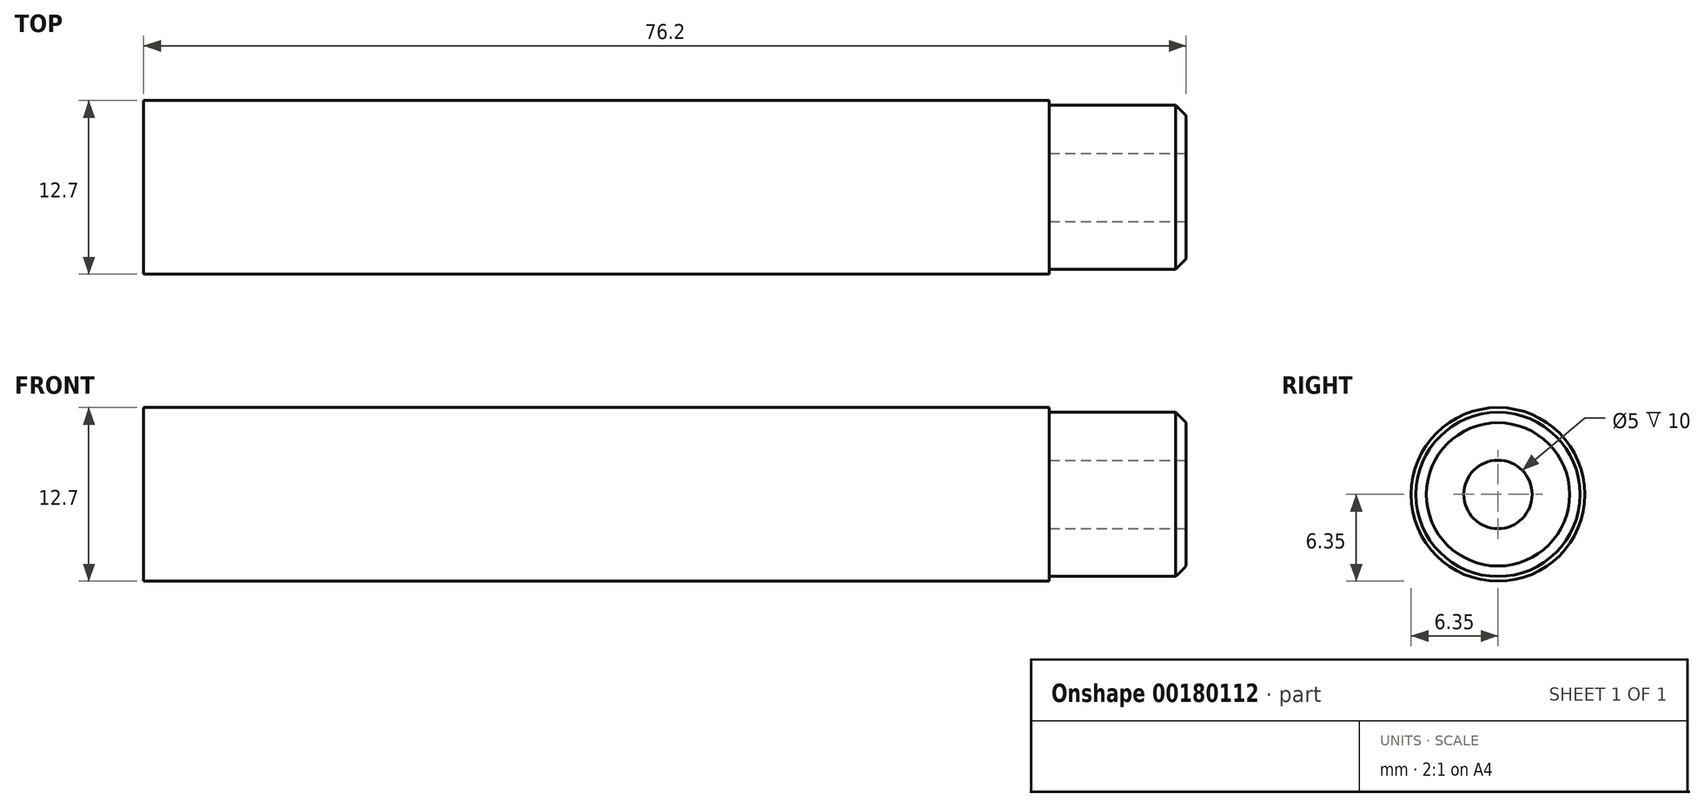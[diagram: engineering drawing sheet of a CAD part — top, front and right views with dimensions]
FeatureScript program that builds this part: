
annotation { "Feature Type Name" : "Feature", "Feature Type Description" : "" }
export const myFeature = defineFeature(function(context is Context, id is Id, definition is map)
    precondition{}
    {
        {
            var Q0;
            Q0=qCreatedBy(makeId("Right.planeOp"),FACE);
            var sketch = newSketch(context, id + "F0", { "sketchPlane" : qUnion([Q0])});
            skCircle(sketch, "E0", {"center": v(0, 0) * mm, "radius": 6 * mm});
            skSolve(sketch);
        }
        {
            var Q0;
            Q0=qSketchRegion(id+"F0",true);
            extrude(context, id + "F1", {"entities" : qUnion([Q0]), "depth" : 76.2 * mm});
        }
        {
            var Q0;
            Q0=makeQuery(id+"F1.opExtrude","CAP_EDGE",EDGE,{"disambiguationData":[OSD([sQuery(id+"F0.wireOp",EDGE,"E0")])],"isStart":false});
            chamfer(context, id + "F2", {"entities" : qUnion([Q0]), "width" : 0.76 * mm, "tangentPropagation" : true});
        }
        {
            var Q0;
            Q0=makeQuery(id+"F1.opExtrude","CAP_FACE",FACE,{"disambiguationData":[OSD([sQuery(id+"F0.wireOp",EDGE,"E0")])],"isStart":false});
            var sketch = newSketch(context, id + "F3", { "sketchPlane" : qUnion([Q0])});
            skPoint(sketch, "E1", {"position": v(0, 0) * mm});
            skSolve(sketch);
        }
        {
            var Q0;
            Q0=sQuery(id+"F3.wireOp",VERTEX,"E1");
            var Q1;
            Q1=makeQuery(id+"F1.opExtrude","SWEPT_BODY",BODY,{"disambiguationData":[OSD([sQuery(id+"F0.wireOp",EDGE,"E0")])]});
            hole(context, id + "F4", {"style" : HoleStyle.SIMPLE, "endStyle" : HoleEndStyle.BLIND, "standardTappedOrClearance" : lookupTablePath({ "standard" : "ISO", "engagement" : "75%", "pitch" : "1 mm", "size" : "M6", "type" : "Tapped" }), "standardBlindInLast" : lookupTablePath({ "standard" : "ISO", "engagement" : "75%", "pitch" : "1 mm", "size" : "M6", "type" : "Tapped" }), "holeDiameter" : 5 * mm, "holeDepth" : 16 * mm, "locations" : qUnion([Q0]), "scope" : qUnion([Q1]), "majorDiameter" : 6 * mm});
        }
        {
            var Q0;
            Q0=makeQuery(id+"F1.opExtrude","CAP_FACE",FACE,{"disambiguationData":[OSD([sQuery(id+"F0.wireOp",EDGE,"E0")])],"isStart":false});
            cPlane(context, id + "F5", {"entities" : qUnion([Q0]), "cplaneType" : CPlaneType.OFFSET, "offset" : 10 * mm, "oppositeDirection" : true, "width" : 152.4 * mm, "height" : 152.4 * mm});
        }
        {
            var Q0;
            Q0=qCreatedBy(id+"F5.planeOp",FACE);
            var sketch = newSketch(context, id + "F6", { "sketchPlane" : qUnion([Q0])});
            skCircle(sketch, "E2", {"center": v(0, 0) * mm, "radius": 6.35 * mm});
            skSolve(sketch);
        }
        {
            var Q0;
            Q0=qSketchRegion(id+"F6",true);
            var Q1;
            Q1=makeQuery(id+"F1.opExtrude","CAP_FACE",FACE,{"disambiguationData":[OSD([sQuery(id+"F0.wireOp",EDGE,"E0")])],"isStart":true});
            extrude(context, id + "F7", {"entities" : qUnion([Q0]), "operationType" : NewBodyOperationType.ADD, "endBound" : BoundingType.UP_TO_SURFACE, "oppositeDirection" : true, "endBoundEntityFace" : qUnion([Q1]), "depth" : 25.4 * mm});
        }
    });
